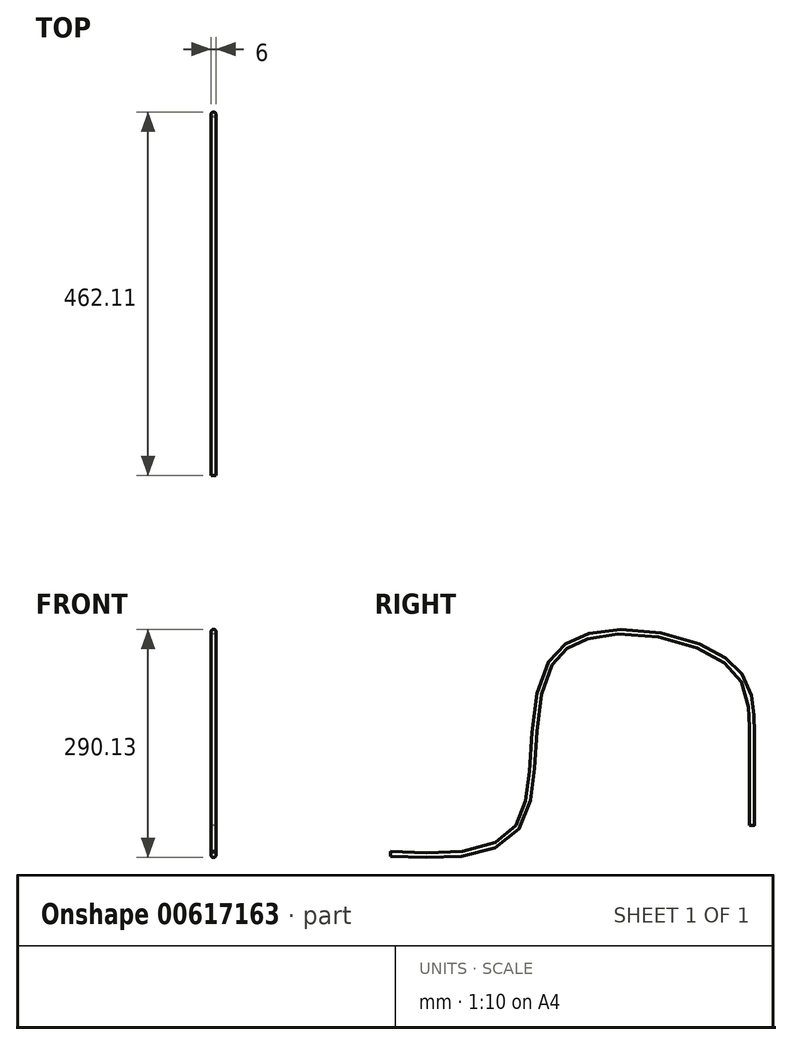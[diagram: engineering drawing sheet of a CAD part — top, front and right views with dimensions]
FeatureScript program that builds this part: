
annotation { "Feature Type Name" : "Feature", "Feature Type Description" : "" }
export const myFeature = defineFeature(function(context is Context, id is Id, definition is map)
    precondition{}
    {
        {
            var Q0;
            Q0=qCreatedBy(makeId("Top.planeOp"),FACE);
            var sketch = newSketch(context, id + "F0", { "sketchPlane" : qUnion([Q0])});
            skCircle(sketch, "E0", {"center": v(0, 0) * mm, "radius": 3 * mm});
            skSolve(sketch);
        }
        {
            var Q0;
            Q0=qCreatedBy(makeId("Right.planeOp"),FACE);
            var sketch = newSketch(context, id + "F1", { "sketchPlane" : qUnion([Q0])});
            skLineSegment(sketch, "E1", {"start": v(0, 2.86) * mm, "end": v(0, 0) * mm});
            skFitSpline(sketch, "E2", {"points": [v(0, 2.86) * mm, v(0, 120.21) * mm, v(-31.95, 208.3) * mm, v(-245.05, 220) * mm, v(-294.57, 2.86) * mm, v(-458.88, -36) * mm], "startDerivative": vector(1.16, 700.36) * mm, "endDerivative": vector(-1008.07, 50.26) * mm});
            skSolve(sketch);
        }
        {
            var Q0;
            Q0=makeQuery(id+"F0.imprint","IMPRINT",FACE,{"disambiguationData":[TD([[makeQuery(id+"F0.imprint","IMPRINT",EDGE,{"derivedFrom":sQuery(id+"F0.wireOp",EDGE,"E0")}),1.0]])]});
            var Q1;
            Q1=sQuery(id+"F0.wireOp",EDGE,"E0");
            var Q2;
            Q2=sQuery(id+"F1.wireOp",EDGE,"46e0c154-bffa-4948-b200-db96d6c28ed3");
            var Q3;
            Q3=sQuery(id+"F1.wireOp",EDGE,"E1");
            var Q4;
            Q4=sQuery(id+"F1.wireOp",EDGE,"E2");
            sweep(context, id + "F2", {"profiles" : qUnion([Q0]), "surfaceProfiles" : qUnion([Q1]), "path" : qUnion([Q2, Q3, Q4])});
        }
    });
